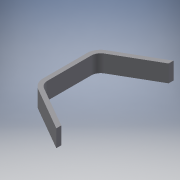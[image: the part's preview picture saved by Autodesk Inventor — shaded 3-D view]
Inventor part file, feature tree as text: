
AUTODESK INVENTOR PART (.ipt)
format: ipt  version: 2016 SP1 (Build 200210100, 210)  size: 103,936 bytes
history: native  units: mm
features: extrude x1, sketch x1
ambient origin geometry x8: Origin, YZ Plane, XZ Plane, XY Plane, X Axis, Y Axis, Z Axis, Center Point
bodies: Solid1 (feature_tree)
feature tree (2):
  extrude  "Extrusion1"  [1 undecoded]
  sketch  "Sketch1"  dims[d4=10.0mm d5=0.0mm]
note: 1 required parameter value undecoded (feature->parameter linkage not recoverable at this tier; creation-order binding heuristic only, values carry confidence <= 0.55)
